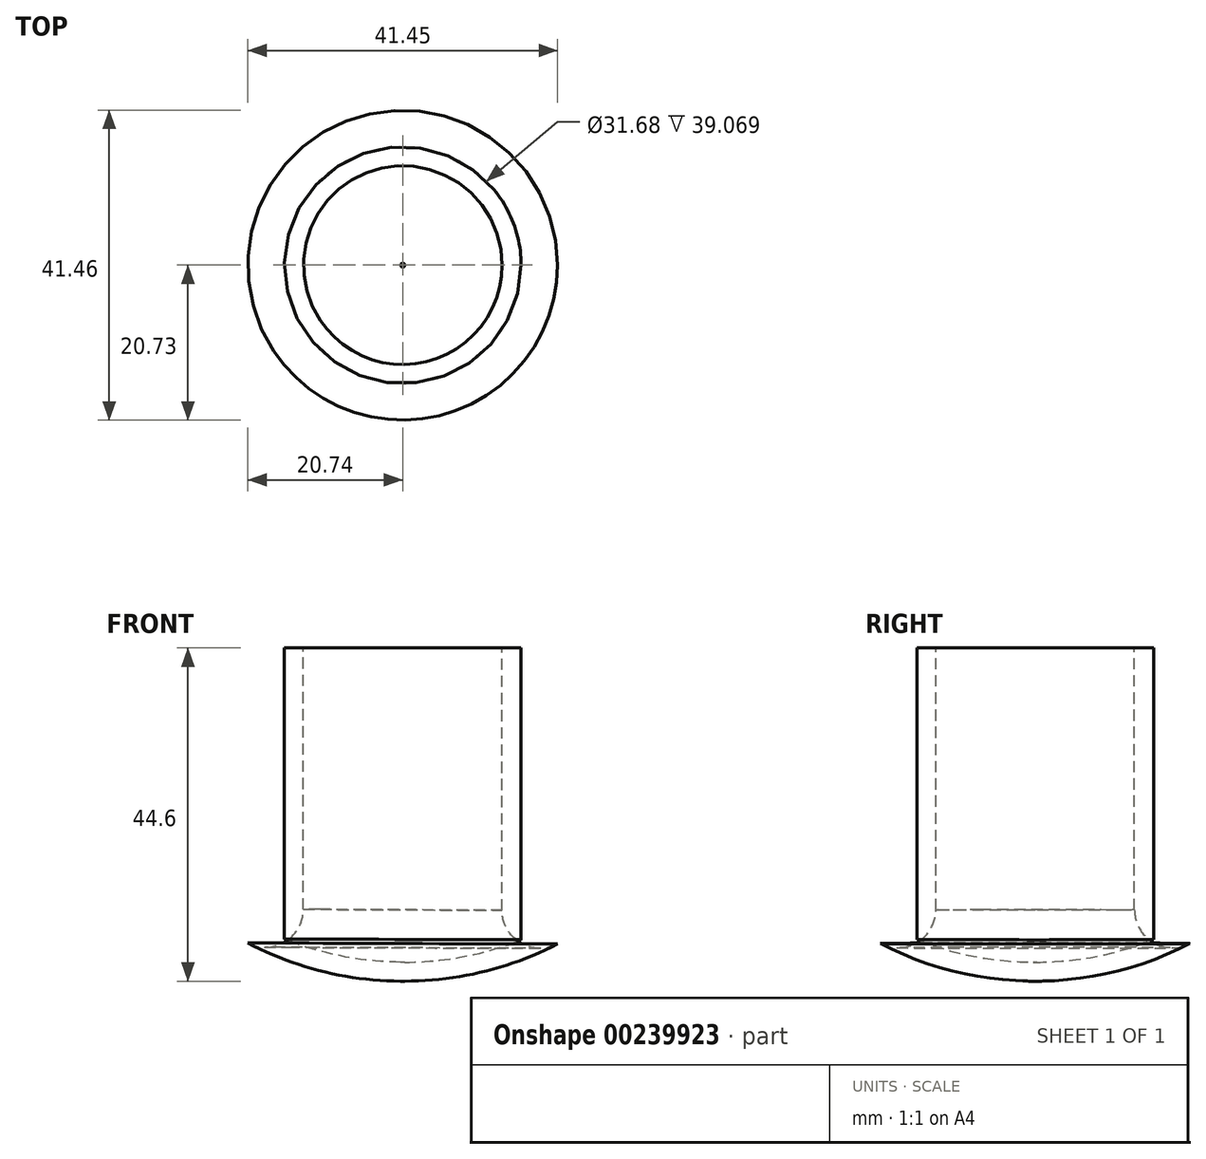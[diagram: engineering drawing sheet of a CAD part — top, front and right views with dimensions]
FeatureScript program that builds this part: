
annotation { "Feature Type Name" : "Feature", "Feature Type Description" : "" }
export const myFeature = defineFeature(function(context is Context, id is Id, definition is map)
    precondition{}
    {
        {
            var Q0;
            Q0=qCreatedBy(makeId("Front.planeOp"),FACE);
            var sketch = newSketch(context, id + "F0", { "sketchPlane" : qUnion([Q0])});
            skArc(sketch, "E0", {"start": v(0.28, 44.6) * mm, "mid": v(-44.6, 0.15) * mm, "end": v(-0.02, -44.6) * mm});
            skLineSegment(sketch, "E1", {"start": v(0.28, 44.6) * mm, "end": v(-0.02, -44.6) * mm});
            skSolve(sketch);
        }
        {
            var Q0;
            Q0=makeQuery(id+"F0.imprint","IMPRINT",FACE,{"disambiguationData":[TD([[makeQuery(id+"F0.imprint","IMPRINT",EDGE,{"derivedFrom":sQuery(id+"F0.wireOp",EDGE,"E0")}),1.0]])]});
            var Q1;
            Q1=sQuery(id+"F0.wireOp",EDGE,"E1");
            revolve(context, id + "F1", {"entities" : qUnion([Q0]), "axis" : qUnion([Q1]), "revolveType" : RevolveType.FULL});
        }
        {
            var Q0;
            Q0=qCreatedBy(makeId("Top.planeOp"),FACE);
            var sketch = newSketch(context, id + "F2", { "sketchPlane" : qUnion([Q0])});
            skCircle(sketch, "E2", {"center": v(0, 0) * mm, "radius": 13.3 * mm});
            skSolve(sketch);
        }
        {
            var Q0;
            Q0 = qSketchRegion(id + "F2", true);
            extrude(context, id + "F3", {"entities" : qUnion([Q0]), "operationType" : NewBodyOperationType.REMOVE, "oppositeDirection" : true, "depth" : 126.75 * mm});
        }
        {
            var Q0;
            Q0=makeQuery(id+"F3.boolean.opBoolean","COPY",FACE,{"derivedFrom":makeQuery(id+"F3.opExtrude","CAP_FACE",FACE,{"disambiguationData":[OSD([sQuery(id+"F2.wireOp",EDGE,"E2")])],"isStart":true})});
            shell(context, id + "F4", {"entities" : qUnion([Q0]), "thickness" : 2.54 * mm});
        }
        {
            var Q0;
            Q0=makeQuery(id+"F3.boolean.opBoolean","INTERSECT",EDGE,{"derivedFrom":[makeQuery(id+"F1.opRevolve","SWEPT_FACE",FACE,{"disambiguationData":[OSD([sQuery(id+"F0.wireOp",EDGE,"E0")])]}),makeQuery(id+"F3.opExtrude","SWEPT_FACE",FACE,{"disambiguationData":[OSD([sQuery(id+"F2.wireOp",EDGE,"E2")])]})]});
            fillet(context, id + "F5", {"entities" : qUnion([Q0]), "radius" : 5.08 * mm, "tangentPropagation" : true, "allowEdgeOverflow" : false});
        }
    });
